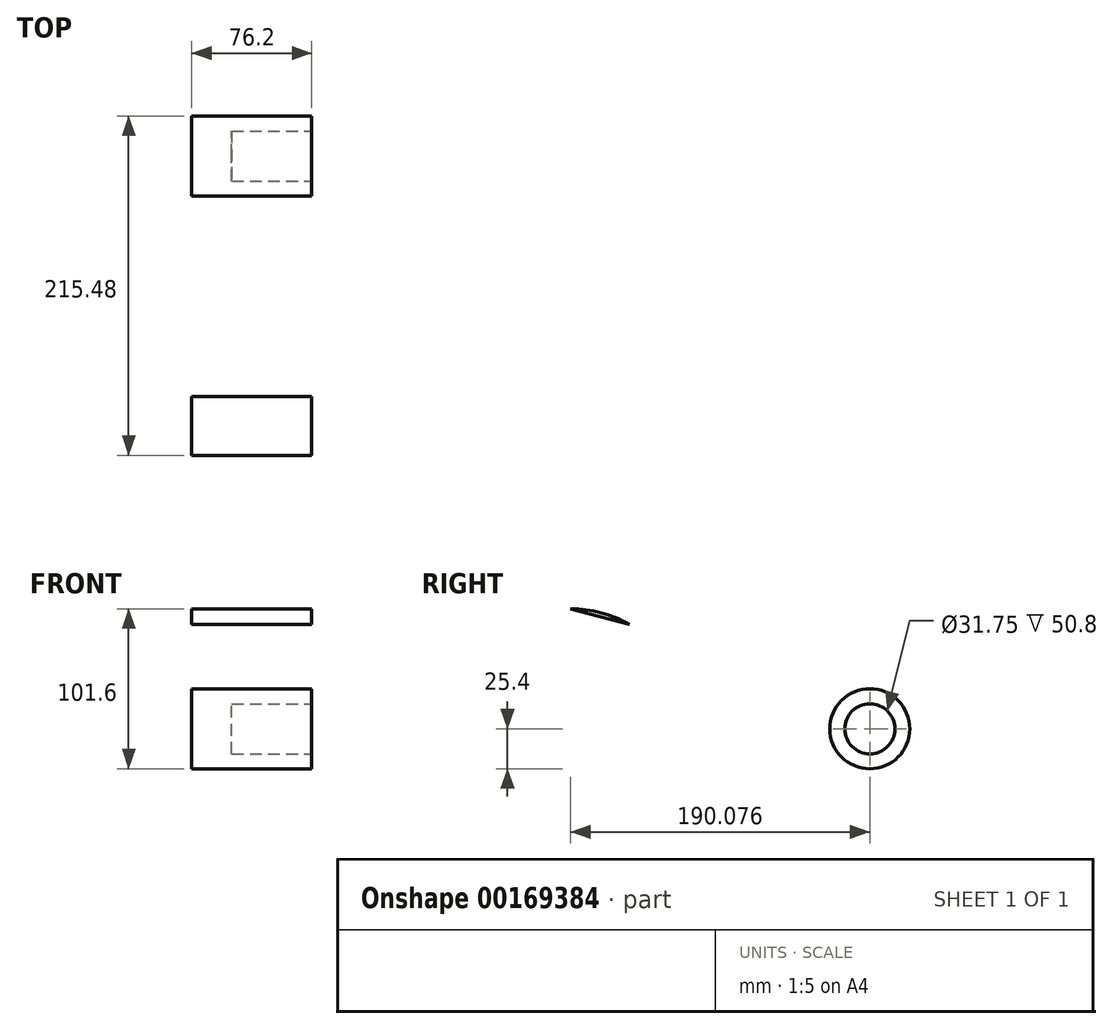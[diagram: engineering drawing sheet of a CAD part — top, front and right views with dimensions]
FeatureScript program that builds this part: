
annotation { "Feature Type Name" : "Feature", "Feature Type Description" : "" }
export const myFeature = defineFeature(function(context is Context, id is Id, definition is map)
    precondition{}
    {
        {
            var Q0;
            Q0=qCreatedBy(makeId("Right.planeOp"),FACE);
            var sketch = newSketch(context, id + "F0", { "sketchPlane" : qUnion([Q0])});
            skCircle(sketch, "E0", {"center": v(0, 0) * mm, "radius": 76.2 * mm});
            skCircle(sketch, "E1", {"center": v(190.08, 0) * mm, "radius": 25.4 * mm});
            skLineSegment(sketch, "E2", {"start": v(0, 76.2) * mm, "end": v(196.53, 24.57) * mm});
            skLineSegment(sketch, "E3", {"start": v(0, -76.2) * mm, "end": v(196.53, -24.57) * mm});
            skSolve(sketch);
        }
        {
            var Q0;
            {var subQ0=sQuery(id+"F0.wireOp",EDGE,"E2");var subQ1=sQuery(id+"F0.wireOp",EDGE,"E0");var subQ2=makeQuery(id+"F0.imprint","INTERSECT",VERTEX,{"disambiguationData":[OD(0.0)],"derivedFrom":[subQ1,subQ0]});Q0=makeQuery(id+"F0.imprint","IMPRINT",FACE,{"disambiguationData":[TD([[makeQuery(id+"F0.imprint","IMPRINT",EDGE,{"disambiguationData":[TD([[subQ2,-1.0]])],"derivedFrom":subQ1}),1.0]])]});}
            var Q1;
            {var subQ0=sQuery(id+"F0.wireOp",EDGE,"E2");var subQ1=sQuery(id+"F0.wireOp",EDGE,"E0");var subQ2=makeQuery(id+"F0.imprint","INTERSECT",VERTEX,{"disambiguationData":[OD(1.0)],"derivedFrom":[subQ1,subQ0]});Q1=makeQuery(id+"F0.imprint","IMPRINT",FACE,{"disambiguationData":[TD([[makeQuery(id+"F0.imprint","IMPRINT",EDGE,{"disambiguationData":[TD([[subQ2,1.0]])],"derivedFrom":subQ1}),-1.0]])]});}
            var Q2;
            {var subQ0=sQuery(id+"F0.wireOp",EDGE,"E1");var subQ1=makeQuery(id+"F0.imprint","INTERSECT",VERTEX,{"derivedFrom":[subQ0,sQuery(id+"F0.wireOp",EDGE,"E2")]});Q2=makeQuery(id+"F0.imprint","IMPRINT",FACE,{"disambiguationData":[TD([[makeQuery(id+"F0.imprint","IMPRINT",EDGE,{"disambiguationData":[TD([[subQ1,-1.0]])],"derivedFrom":subQ0}),1.0]])]});}
            extrude(context, id + "F1", {"entities" : qUnion([Q0, Q1, Q2]), "depth" : 76.2 * mm});
        }
        {
            var Q0;
            Q0=makeQuery(id+"F1.opExtrude","CAP_FACE",FACE,{"disambiguationData":[OSD([sQuery(id+"F0.wireOp",EDGE,"E0"),sQuery(id+"F0.wireOp",EDGE,"E1"),sQuery(id+"F0.wireOp",EDGE,"E2"),sQuery(id+"F0.wireOp",EDGE,"E3")])],"isStart":false});
            var sketch = newSketch(context, id + "F2", { "sketchPlane" : qUnion([Q0])});
            skCircle(sketch, "E4", {"center": v(0, 0) * mm, "radius": 66.68 * mm});
            skCircle(sketch, "E5", {"center": v(190.08, 0) * mm, "radius": 15.88 * mm});
            skSolve(sketch);
        }
        {
            var Q0;
            Q0=makeQuery(id+"F2.imprint","IMPRINT",FACE,{"disambiguationData":[TD([[makeQuery(id+"F2.imprint","IMPRINT",EDGE,{"derivedFrom":sQuery(id+"F2.wireOp",EDGE,"E4")}),1.0]])]});
            var Q1;
            Q1=makeQuery(id+"F2.imprint","IMPRINT",FACE,{"disambiguationData":[TD([[makeQuery(id+"F2.imprint","IMPRINT",EDGE,{"derivedFrom":sQuery(id+"F2.wireOp",EDGE,"E5")}),1.0]])]});
            extrude(context, id + "F3", {"entities" : qUnion([Q0, Q1]), "operationType" : NewBodyOperationType.REMOVE, "oppositeDirection" : true, "depth" : 50.8 * mm});
        }
    });
